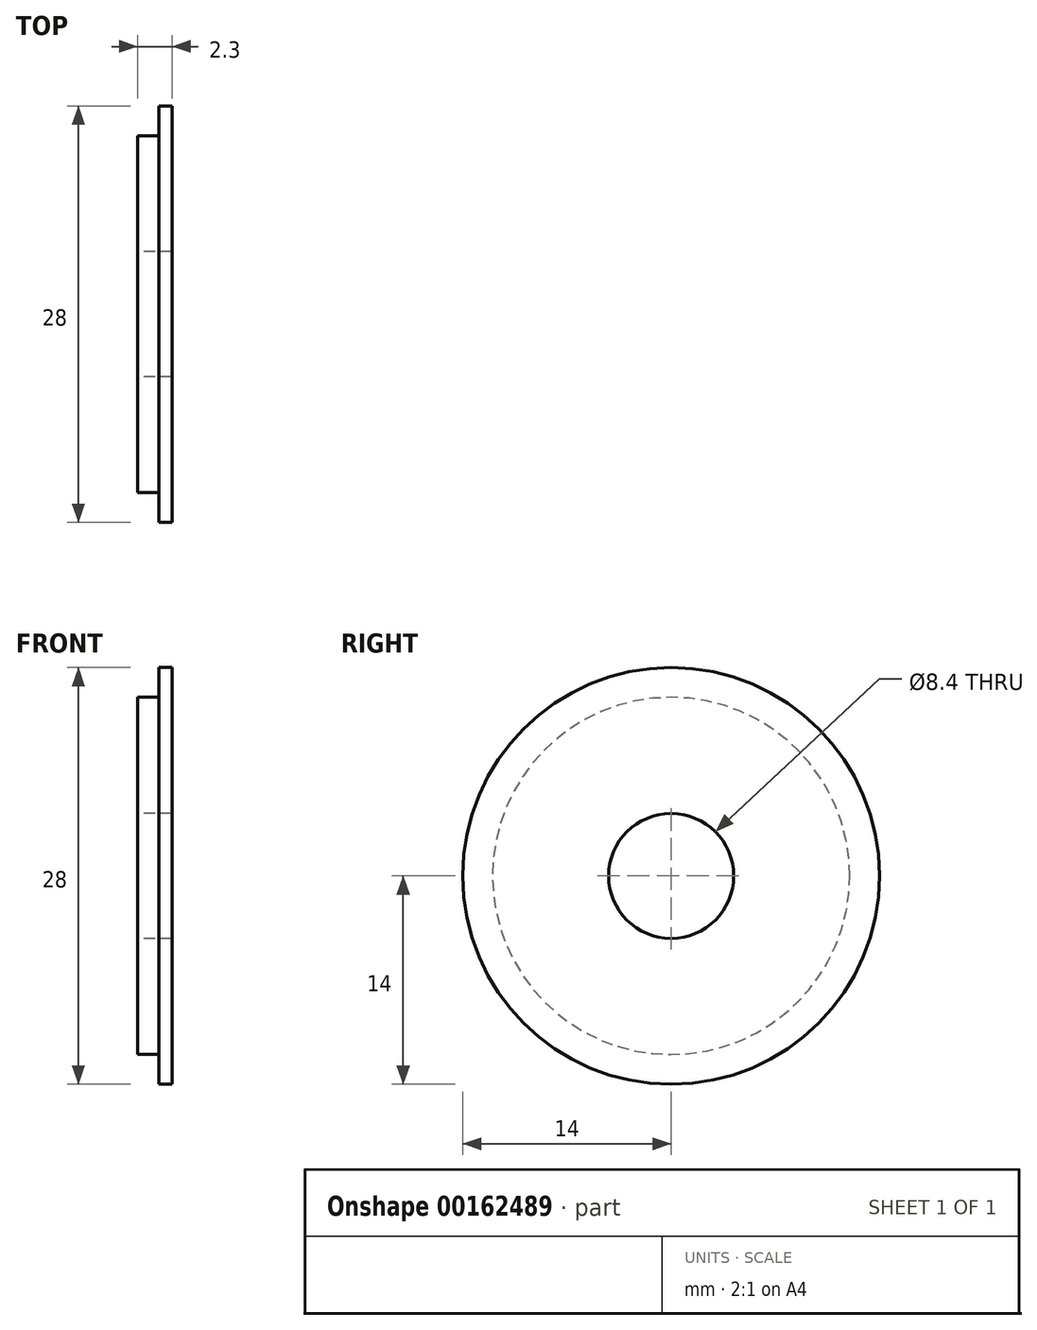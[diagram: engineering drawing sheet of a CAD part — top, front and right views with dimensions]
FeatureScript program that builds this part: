
annotation { "Feature Type Name" : "Feature", "Feature Type Description" : "" }
export const myFeature = defineFeature(function(context is Context, id is Id, definition is map)
    precondition{}
    {
        {
            var Q0;
            Q0=qCreatedBy(makeId("Top.planeOp"),FACE);
            var sketch = newSketch(context, id + "F0", { "sketchPlane" : qUnion([Q0])});
            skLineSegment(sketch, "E0", {"start": v(1.4, 12) * mm, "end": v(0, 12) * mm});
            skLineSegment(sketch, "E1", {"start": v(0, 0) * mm, "end": v(0, 14.26) * mm, "construction": true});
            skLineSegment(sketch, "E2", {"start": v(0, 0) * mm, "end": v(7.98, 0) * mm, "construction": true});
            skLineSegment(sketch, "E3", {"start": v(2.3, 4.2) * mm, "end": v(0, 4.2) * mm});
            skLineSegment(sketch, "E4", {"start": v(1.4, 12) * mm, "end": v(1.4, 14) * mm});
            skLineSegment(sketch, "E5", {"start": v(1.4, 14) * mm, "end": v(2.3, 14) * mm});
            skLineSegment(sketch, "E6", {"start": v(2.3, 14) * mm, "end": v(2.3, 4.2) * mm});
            skLineSegment(sketch, "E7", {"start": v(0, 12) * mm, "end": v(0, 4.2) * mm});
            skSolve(sketch);
        }
        {
            var Q0;
            Q0=qSketchRegion(id+"F0",true);
            var Q1;
            Q1=sQuery(id+"F0.wireOp",EDGE,"E2");
            revolve(context, id + "F1", {"entities" : qUnion([Q0]), "axis" : qUnion([Q1]), "revolveType" : RevolveType.FULL});
        }
    });
